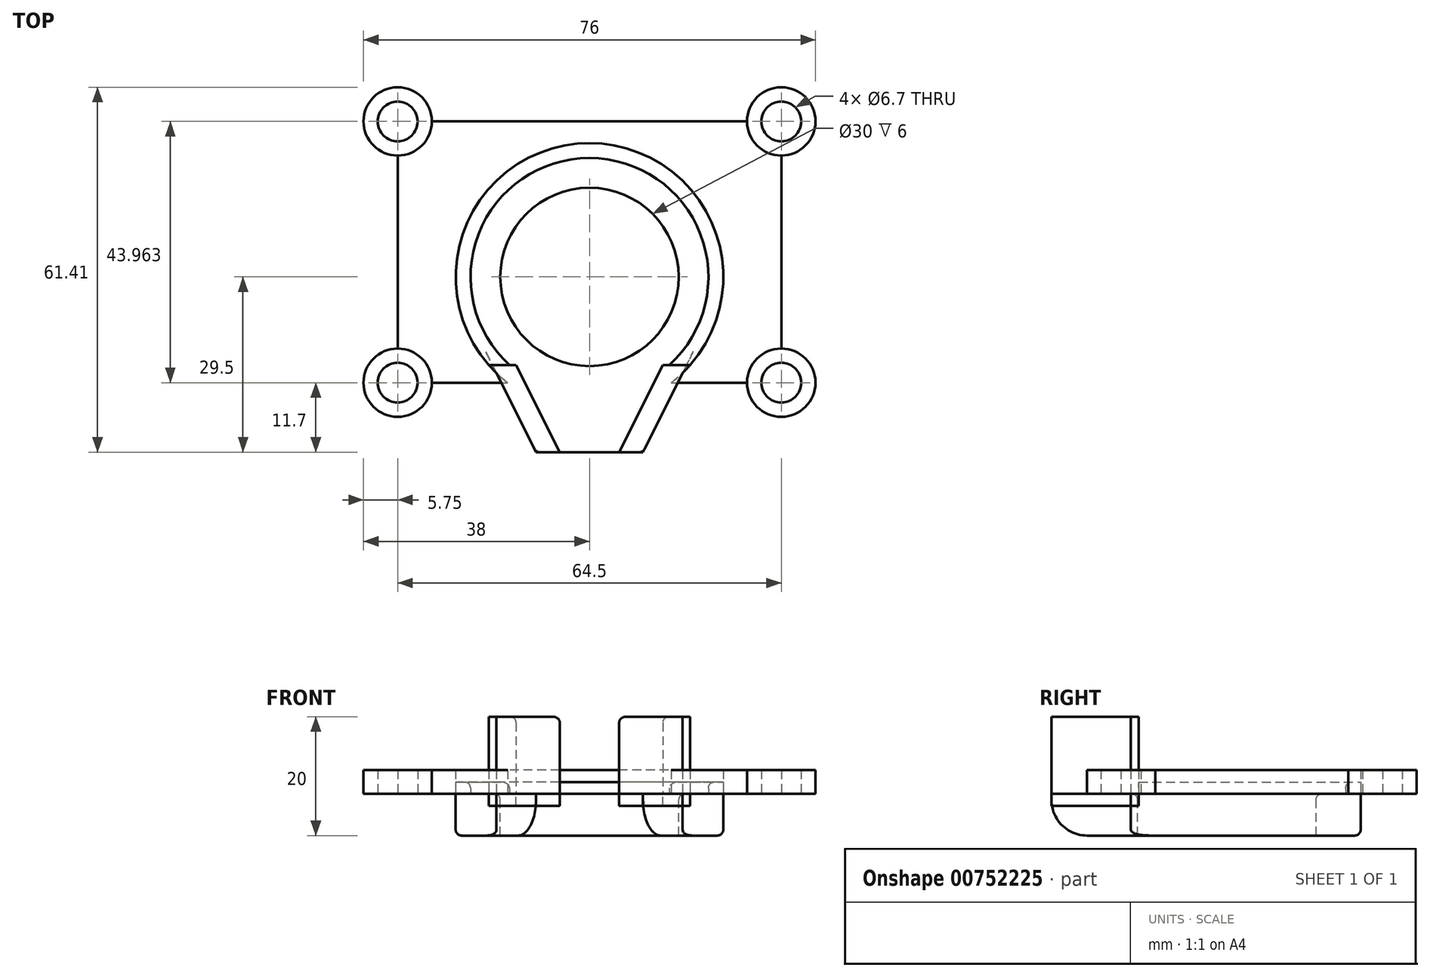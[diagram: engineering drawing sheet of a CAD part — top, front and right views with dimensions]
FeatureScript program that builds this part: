
annotation { "Feature Type Name" : "Feature", "Feature Type Description" : "" }
export const myFeature = defineFeature(function(context is Context, id is Id, definition is map)
    precondition{}
    {
        {
            var Q0;
            Q0=qCreatedBy(makeId("Top.planeOp"),FACE);
            var sketch = newSketch(context, id + "F0", { "sketchPlane" : qUnion([Q0])});
            skCircle(sketch, "E0", {"center": v(-32.25, 26.16) * mm, "radius": 5.75 * mm});
            skCircle(sketch, "E1", {"center": v(32.25, -17.8) * mm, "radius": 5.75 * mm});
            skCircle(sketch, "E2", {"center": v(32.25, -17.8) * mm, "radius": 3.35 * mm});
            skCircle(sketch, "E3", {"center": v(-32.25, 26.16) * mm, "radius": 3.35 * mm});
            skCircle(sketch, "E4", {"center": v(0, 0) * mm, "radius": 20 * mm});
            skCircle(sketch, "E5", {"center": v(0, 0) * mm, "radius": 15 * mm});
            skLineSegment(sketch, "E6", {"start": v(-32.25, -17.8) * mm, "end": v(32.25, -17.8) * mm});
            skCircle(sketch, "E7", {"center": v(-32.25, -17.8) * mm, "radius": 5.75 * mm});
            skCircle(sketch, "E8", {"center": v(-32.25, -17.8) * mm, "radius": 3.35 * mm});
            skLineSegment(sketch, "E9", {"start": v(-32.25, 26.16) * mm, "end": v(32.25, 26.16) * mm});
            skCircle(sketch, "E10", {"center": v(32.25, 26.16) * mm, "radius": 5.75 * mm});
            skCircle(sketch, "E11", {"center": v(32.25, 26.16) * mm, "radius": 3.35 * mm});
            skLineSegment(sketch, "E12", {"start": v(-5, -29.5) * mm, "end": v(5, -29.5) * mm});
            skLineSegment(sketch, "E13", {"start": v(-5, -29.5) * mm, "end": v(-9, -29.5) * mm});
            skLineSegment(sketch, "E14", {"start": v(5, -29.5) * mm, "end": v(9, -29.5) * mm});
            skLineSegment(sketch, "E15", {"start": v(-5, -29.5) * mm, "end": v(-12.33, -14.82) * mm});
            skLineSegment(sketch, "E16", {"start": v(-12.33, -14.82) * mm, "end": v(12.33, -14.82) * mm});
            skLineSegment(sketch, "E17", {"start": v(12.33, -14.82) * mm, "end": v(5, -29.5) * mm});
            skLineSegment(sketch, "E18", {"start": v(-12.33, -14.82) * mm, "end": v(-16.33, -14.82) * mm});
            skLineSegment(sketch, "E19", {"start": v(-16.33, -14.82) * mm, "end": v(-9, -29.5) * mm});
            skLineSegment(sketch, "E20", {"start": v(9, -29.5) * mm, "end": v(16.32, -14.82) * mm});
            skLineSegment(sketch, "E21", {"start": v(16.32, -14.82) * mm, "end": v(12.33, -14.82) * mm});
            skCircle(sketch, "E22", {"center": v(0, 0) * mm, "radius": 22.5 * mm});
            skLineSegment(sketch, "E23", {"start": v(-32.25, -17.8) * mm, "end": v(-32.25, 0) * mm});
            skLineSegment(sketch, "E24", {"start": v(-32.25, 0) * mm, "end": v(-32.25, 26.16) * mm});
            skLineSegment(sketch, "E25", {"start": v(-32.25, 26.16) * mm, "end": v(32.25, -17.8) * mm});
            skPoint(sketch, "E26.trimOffspring.end.orphan", {"position": v(0, -29.5) * mm});
            skLineSegment(sketch, "E27", {"start": v(0, -29.5) * mm, "end": v(0, 26.16) * mm});
            skLineSegment(sketch, "E28", {"start": v(32.25, 26.16) * mm, "end": v(32.25, 0) * mm});
            skLineSegment(sketch, "E29", {"start": v(32.25, 0) * mm, "end": v(32.25, -17.8) * mm});
            skLineSegment(sketch, "E30", {"start": v(-16.33, -14.82) * mm, "end": v(-16.93, -14.82) * mm});
            skLineSegment(sketch, "E31", {"start": v(16.32, -14.82) * mm, "end": v(16.93, -14.82) * mm});
            skSolve(sketch);
        }
        {
            var Q0;
            {var subQ0=sQuery(id+"F0.wireOp",EDGE,"E7");var subQ1=sQuery(id+"F0.wireOp",EDGE,"Wz8c8u1L-tIaJ-pxJv-zDBa-IqU4CHtZDm8W");var subQ2=makeQuery(id+"F0.imprint","INTERSECT",VERTEX,{"derivedFrom":[subQ1,subQ0]});Q0=makeQuery(id+"F0.imprint","IMPRINT",FACE,{"disambiguationData":[TD([[makeQuery(id+"F0.imprint","IMPRINT",EDGE,{"disambiguationData":[TD([[subQ2,-1.0]])],"derivedFrom":subQ1}),-1.0]])]});}
            var Q1;
            {var subQ0=sQuery(id+"F0.wireOp",EDGE,"E10");var subQ1=sQuery(id+"F0.wireOp",EDGE,"E9");var subQ2=makeQuery(id+"F0.imprint","INTERSECT",VERTEX,{"derivedFrom":[subQ1,subQ0]});Q1=makeQuery(id+"F0.imprint","IMPRINT",FACE,{"disambiguationData":[TD([[makeQuery(id+"F0.imprint","IMPRINT",EDGE,{"disambiguationData":[TD([[subQ2,-1.0]])],"derivedFrom":subQ1}),1.0]])]});}
            var Q2;
            {var subQ0=sQuery(id+"F0.wireOp",EDGE,"Wz8c8u1L-tIaJ-pxJv-zDBa-IqU4CHtZDm8W");var subQ1=sQuery(id+"F0.wireOp",EDGE,"E0");var subQ2=makeQuery(id+"F0.imprint","INTERSECT",VERTEX,{"derivedFrom":[subQ1,subQ0]});Q2=makeQuery(id+"F0.imprint","IMPRINT",FACE,{"disambiguationData":[TD([[makeQuery(id+"F0.imprint","IMPRINT",EDGE,{"disambiguationData":[TD([[subQ2,1.0]])],"derivedFrom":subQ1}),1.0]])]});}
            var Q3;
            {var subQ0=sQuery(id+"F0.wireOp",EDGE,"lU8kgJ5v-FxIN-fgI9-XZON-ElkpLmHzZSri");var subQ1=sQuery(id+"F0.wireOp",EDGE,"E1");var subQ2=makeQuery(id+"F0.imprint","INTERSECT",VERTEX,{"derivedFrom":[subQ1,subQ0]});Q3=makeQuery(id+"F0.imprint","IMPRINT",FACE,{"disambiguationData":[TD([[makeQuery(id+"F0.imprint","IMPRINT",EDGE,{"disambiguationData":[TD([[subQ2,1.0]])],"derivedFrom":subQ1}),1.0]])]});}
            var Q4;
            {var subQ0=sQuery(id+"F0.wireOp",EDGE,"E7");var subQ1=sQuery(id+"F0.wireOp",EDGE,"Wz8c8u1L-tIaJ-pxJv-zDBa-IqU4CHtZDm8W");var subQ2=makeQuery(id+"F0.imprint","INTERSECT",VERTEX,{"derivedFrom":[subQ1,subQ0]});Q4=makeQuery(id+"F0.imprint","IMPRINT",FACE,{"disambiguationData":[TD([[makeQuery(id+"F0.imprint","IMPRINT",EDGE,{"disambiguationData":[TD([[subQ2,-1.0]])],"derivedFrom":subQ1}),1.0]])]});}
            var Q5;
            {var subQ0=sQuery(id+"F0.wireOp",EDGE,"E10");var subQ1=sQuery(id+"F0.wireOp",EDGE,"E9");var subQ2=makeQuery(id+"F0.imprint","INTERSECT",VERTEX,{"derivedFrom":[subQ1,subQ0]});Q5=makeQuery(id+"F0.imprint","IMPRINT",FACE,{"disambiguationData":[TD([[makeQuery(id+"F0.imprint","IMPRINT",EDGE,{"disambiguationData":[TD([[subQ2,-1.0]])],"derivedFrom":subQ1}),-1.0]])]});}
            var Q6;
            {var subQ0=sQuery(id+"F0.wireOp",EDGE,"Wz8c8u1L-tIaJ-pxJv-zDBa-IqU4CHtZDm8W");var subQ1=sQuery(id+"F0.wireOp",EDGE,"E0");var subQ2=makeQuery(id+"F0.imprint","INTERSECT",VERTEX,{"derivedFrom":[subQ1,subQ0]});Q6=makeQuery(id+"F0.imprint","IMPRINT",FACE,{"disambiguationData":[TD([[makeQuery(id+"F0.imprint","IMPRINT",EDGE,{"disambiguationData":[TD([[subQ2,-1.0]])],"derivedFrom":subQ1}),1.0]])]});}
            var Q7;
            {var subQ0=sQuery(id+"F0.wireOp",EDGE,"E9");var subQ1=sQuery(id+"F0.wireOp",EDGE,"E0");var subQ2=makeQuery(id+"F0.imprint","INTERSECT",VERTEX,{"derivedFrom":[subQ1,subQ0]});Q7=makeQuery(id+"F0.imprint","IMPRINT",FACE,{"disambiguationData":[TD([[makeQuery(id+"F0.imprint","IMPRINT",EDGE,{"disambiguationData":[TD([[subQ2,1.0]])],"derivedFrom":subQ1}),1.0]])]});}
            var Q8;
            {var subQ0=sQuery(id+"F0.wireOp",EDGE,"lU8kgJ5v-FxIN-fgI9-XZON-ElkpLmHzZSri");var subQ1=sQuery(id+"F0.wireOp",EDGE,"E1");var subQ2=makeQuery(id+"F0.imprint","INTERSECT",VERTEX,{"derivedFrom":[subQ1,subQ0]});Q8=makeQuery(id+"F0.imprint","IMPRINT",FACE,{"disambiguationData":[TD([[makeQuery(id+"F0.imprint","IMPRINT",EDGE,{"disambiguationData":[TD([[subQ2,-1.0]])],"derivedFrom":subQ1}),1.0]])]});}
            var Q9;
            {var subQ0=sQuery(id+"F0.wireOp",EDGE,"E6");var subQ1=sQuery(id+"F0.wireOp",EDGE,"E1");var subQ2=makeQuery(id+"F0.imprint","INTERSECT",VERTEX,{"derivedFrom":[subQ1,subQ0]});Q9=makeQuery(id+"F0.imprint","IMPRINT",FACE,{"disambiguationData":[TD([[makeQuery(id+"F0.imprint","IMPRINT",EDGE,{"disambiguationData":[TD([[subQ2,1.0]])],"derivedFrom":subQ1}),1.0]])]});}
            var Q10;
            {var subQ0=sQuery(id+"F0.wireOp",EDGE,"E7");var subQ1=sQuery(id+"F0.wireOp",EDGE,"E6");var subQ2=makeQuery(id+"F0.imprint","INTERSECT",VERTEX,{"derivedFrom":[subQ1,subQ0]});Q10=makeQuery(id+"F0.imprint","IMPRINT",FACE,{"disambiguationData":[TD([[makeQuery(id+"F0.imprint","IMPRINT",EDGE,{"disambiguationData":[TD([[subQ2,1.0]])],"derivedFrom":subQ1}),-1.0]])]});}
            var Q11;
            {var subQ0=sQuery(id+"F0.wireOp",EDGE,"E7");var subQ1=sQuery(id+"F0.wireOp",EDGE,"E6");var subQ2=makeQuery(id+"F0.imprint","INTERSECT",VERTEX,{"derivedFrom":[subQ1,subQ0]});Q11=makeQuery(id+"F0.imprint","IMPRINT",FACE,{"disambiguationData":[TD([[makeQuery(id+"F0.imprint","IMPRINT",EDGE,{"disambiguationData":[TD([[subQ2,1.0]])],"derivedFrom":subQ1}),1.0]])]});}
            extrude(context, id + "F1", {"entities" : qUnion([Q0, Q1, Q2, Q3, Q4, Q5, Q6, Q7, Q8, Q9, Q10, Q11]), "depth" : 4 * mm, "offsetDistance" : 25 * mm});
        }
        {
            var Q0;
            {var subQ5=sQuery(id+"F0.wireOp",EDGE,"Wz8c8u1L-tIaJ-pxJv-zDBa-IqU4CHtZDm8W");var subQ6=sQuery(id+"F0.wireOp",EDGE,"E0");var subQ7=makeQuery(id+"F0.imprint","INTERSECT",VERTEX,{"derivedFrom":[subQ6,subQ5]});Q0=makeQuery(id+"F0.imprint","IMPRINT",FACE,{"disambiguationData":[TD([[makeQuery(id+"F0.imprint","IMPRINT",EDGE,{"disambiguationData":[TD([[subQ7,-1.0]])],"derivedFrom":subQ6}),-1.0]])]});}
            var Q1;
            {var subQ5=sQuery(id+"F0.wireOp",EDGE,"E0");var subQ10=sQuery(id+"F0.wireOp",EDGE,"E9");var subQ11=makeQuery(id+"F0.imprint","INTERSECT",VERTEX,{"derivedFrom":[subQ5,subQ10]});Q1=makeQuery(id+"F0.imprint","IMPRINT",FACE,{"disambiguationData":[TD([[makeQuery(id+"F0.imprint","IMPRINT",EDGE,{"disambiguationData":[TD([[subQ11,1.0]])],"derivedFrom":subQ5}),-1.0]])]});}
            var Q2;
            {var subQ1=sQuery(id+"F0.wireOp",EDGE,"E6");var subQ5=sQuery(id+"F0.wireOp",EDGE,"E1");var subQ6=makeQuery(id+"F0.imprint","INTERSECT",VERTEX,{"derivedFrom":[subQ5,subQ1]});Q2=makeQuery(id+"F0.imprint","IMPRINT",FACE,{"disambiguationData":[TD([[makeQuery(id+"F0.imprint","IMPRINT",EDGE,{"disambiguationData":[TD([[subQ6,1.0]])],"derivedFrom":subQ5}),-1.0]])]});}
            var Q3;
            {var subQ0=sQuery(id+"F0.wireOp",EDGE,"E19");var subQ1=sQuery(id+"F0.wireOp",EDGE,"E6");var subQ2=makeQuery(id+"F0.imprint","INTERSECT",VERTEX,{"derivedFrom":[subQ1,subQ0]});Q3=makeQuery(id+"F0.imprint","IMPRINT",FACE,{"disambiguationData":[TD([[makeQuery(id+"F0.imprint","IMPRINT",EDGE,{"disambiguationData":[TD([[subQ2,-1.0]])],"derivedFrom":subQ1}),1.0]])]});}
            var Q4;
            {var subQ9=sQuery(id+"F0.wireOp",EDGE,"E24");var subQ10=sQuery(id+"F0.wireOp",EDGE,"E0");var subQ11=makeQuery(id+"F0.imprint","INTERSECT",VERTEX,{"derivedFrom":[subQ10,subQ9]});Q4=makeQuery(id+"F0.imprint","IMPRINT",FACE,{"disambiguationData":[TD([[makeQuery(id+"F0.imprint","IMPRINT",EDGE,{"disambiguationData":[TD([[subQ11,-1.0]])],"derivedFrom":subQ10}),-1.0]])]});}
            var Q5;
            {var subQ5=sQuery(id+"F0.wireOp",EDGE,"E29");var subQ6=sQuery(id+"F0.wireOp",EDGE,"E1");var subQ7=makeQuery(id+"F0.imprint","INTERSECT",VERTEX,{"derivedFrom":[subQ6,subQ5]});Q5=makeQuery(id+"F0.imprint","IMPRINT",FACE,{"disambiguationData":[TD([[makeQuery(id+"F0.imprint","IMPRINT",EDGE,{"disambiguationData":[TD([[subQ7,-1.0]])],"derivedFrom":subQ6}),-1.0]])]});}
            var Q6;
            {var subQ0=sQuery(id+"F0.wireOp",EDGE,"E20");var subQ1=sQuery(id+"F0.wireOp",EDGE,"E6");var subQ2=makeQuery(id+"F0.imprint","INTERSECT",VERTEX,{"derivedFrom":[subQ1,subQ0]});Q6=makeQuery(id+"F0.imprint","IMPRINT",FACE,{"disambiguationData":[TD([[makeQuery(id+"F0.imprint","IMPRINT",EDGE,{"disambiguationData":[TD([[subQ2,1.0]])],"derivedFrom":subQ1}),1.0]])]});}
            extrude(context, id + "F2", {"entities" : qUnion([Q0, Q1, Q2, Q3, Q4, Q5, Q6]), "depth" : 4 * mm, "offsetDistance" : 25 * mm});
        }
        {
            var Q0;
            {var subQ5=sQuery(id+"F0.wireOp",EDGE,"E30");Q0=makeQuery(id+"F0.imprint","IMPRINT",FACE,{"disambiguationData":[TD([[makeQuery(id+"F0.imprint","IMPRINT",EDGE,{"derivedFrom":subQ5}),-1.0]])]});}
            var Q1;
            {var subQ3=sQuery(id+"F0.wireOp",EDGE,"E4");var subQ7=sQuery(id+"F0.wireOp",EDGE,"E25");var subQ9=makeQuery(id+"F0.imprint","INTERSECT",VERTEX,{"disambiguationData":[OD(0.0)],"derivedFrom":[subQ3,subQ7]});Q1=makeQuery(id+"F0.imprint","IMPRINT",FACE,{"disambiguationData":[TD([[makeQuery(id+"F0.imprint","IMPRINT",EDGE,{"disambiguationData":[TD([[subQ9,-1.0]])],"derivedFrom":subQ3}),1.0]])]});}
            var Q2;
            {var subQ0=sQuery(id+"F0.wireOp",EDGE,"E25");var subQ1=sQuery(id+"F0.wireOp",EDGE,"E4");var subQ2=makeQuery(id+"F0.imprint","INTERSECT",VERTEX,{"disambiguationData":[OD(0.0)],"derivedFrom":[subQ1,subQ0]});Q2=makeQuery(id+"F0.imprint","IMPRINT",FACE,{"disambiguationData":[TD([[makeQuery(id+"F0.imprint","IMPRINT",EDGE,{"disambiguationData":[TD([[subQ2,1.0]])],"derivedFrom":subQ1}),-1.0]])]});}
            var Q3;
            {var subQ0=sQuery(id+"F0.wireOp",EDGE,"E27");var subQ1=sQuery(id+"F0.wireOp",EDGE,"E4");var subQ2=makeQuery(id+"F0.imprint","INTERSECT",VERTEX,{"disambiguationData":[OD(0.0)],"derivedFrom":[subQ1,subQ0]});Q3=makeQuery(id+"F0.imprint","IMPRINT",FACE,{"disambiguationData":[TD([[makeQuery(id+"F0.imprint","IMPRINT",EDGE,{"disambiguationData":[TD([[subQ2,1.0]])],"derivedFrom":subQ1}),-1.0]])]});}
            var Q4;
            {var subQ0=sQuery(id+"F0.wireOp",EDGE,"E27");var subQ1=sQuery(id+"F0.wireOp",EDGE,"E4");var subQ2=makeQuery(id+"F0.imprint","INTERSECT",VERTEX,{"disambiguationData":[OD(0.0)],"derivedFrom":[subQ1,subQ0]});Q4=makeQuery(id+"F0.imprint","IMPRINT",FACE,{"disambiguationData":[TD([[makeQuery(id+"F0.imprint","IMPRINT",EDGE,{"disambiguationData":[TD([[subQ2,1.0]])],"derivedFrom":subQ1}),1.0]])]});}
            var Q5;
            {var subQ0=sQuery(id+"F0.wireOp",EDGE,"E25");var subQ1=sQuery(id+"F0.wireOp",EDGE,"E4");var subQ2=makeQuery(id+"F0.imprint","INTERSECT",VERTEX,{"disambiguationData":[OD(0.0)],"derivedFrom":[subQ1,subQ0]});Q5=makeQuery(id+"F0.imprint","IMPRINT",FACE,{"disambiguationData":[TD([[makeQuery(id+"F0.imprint","IMPRINT",EDGE,{"disambiguationData":[TD([[subQ2,1.0]])],"derivedFrom":subQ1}),1.0]])]});}
            var Q6;
            {var subQ0=sQuery(id+"F0.wireOp",EDGE,"E21");var subQ5=sQuery(id+"F0.wireOp",EDGE,"E4");var subQ6=makeQuery(id+"F0.imprint","INTERSECT",VERTEX,{"derivedFrom":[subQ5,subQ0]});Q6=makeQuery(id+"F0.imprint","IMPRINT",FACE,{"disambiguationData":[TD([[makeQuery(id+"F0.imprint","IMPRINT",EDGE,{"disambiguationData":[TD([[subQ6,-1.0]])],"derivedFrom":subQ5}),1.0]])]});}
            var Q7;
            {var subQ7=sQuery(id+"F0.wireOp",EDGE,"E31");Q7=makeQuery(id+"F0.imprint","IMPRINT",FACE,{"disambiguationData":[TD([[makeQuery(id+"F0.imprint","IMPRINT",EDGE,{"derivedFrom":subQ7}),1.0]])]});}
            var Q8;
            {var subQ1=sQuery(id+"F0.wireOp",EDGE,"E15");var subQ3=sQuery(id+"F0.wireOp",EDGE,"E4");var subQ4=makeQuery(id+"F0.imprint","INTERSECT",VERTEX,{"derivedFrom":[subQ3,subQ1]});Q8=makeQuery(id+"F0.imprint","IMPRINT",FACE,{"disambiguationData":[TD([[makeQuery(id+"F0.imprint","IMPRINT",EDGE,{"disambiguationData":[TD([[subQ4,-1.0]])],"derivedFrom":subQ3}),1.0]])]});}
            var Q9;
            {var subQ5=sQuery(id+"F0.wireOp",EDGE,"E6");var subQ6=sQuery(id+"F0.wireOp",EDGE,"E4");var subQ7=makeQuery(id+"F0.imprint","INTERSECT",VERTEX,{"disambiguationData":[OD(1.0)],"derivedFrom":[subQ6,subQ5]});Q9=makeQuery(id+"F0.imprint","IMPRINT",FACE,{"disambiguationData":[TD([[makeQuery(id+"F0.imprint","IMPRINT",EDGE,{"disambiguationData":[TD([[subQ7,-1.0]])],"derivedFrom":subQ6}),1.0]])]});}
            var Q10;
            {var subQ1=sQuery(id+"F0.wireOp",EDGE,"E18");var subQ3=sQuery(id+"F0.wireOp",EDGE,"E4");var subQ4=makeQuery(id+"F0.imprint","INTERSECT",VERTEX,{"derivedFrom":[subQ3,subQ1]});Q10=makeQuery(id+"F0.imprint","IMPRINT",FACE,{"disambiguationData":[TD([[makeQuery(id+"F0.imprint","IMPRINT",EDGE,{"disambiguationData":[TD([[subQ4,-1.0]])],"derivedFrom":subQ3}),-1.0]])]});}
            var Q11;
            {var subQ0=sQuery(id+"F0.wireOp",EDGE,"E18");var subQ1=sQuery(id+"F0.wireOp",EDGE,"E4");var subQ2=makeQuery(id+"F0.imprint","INTERSECT",VERTEX,{"derivedFrom":[subQ1,subQ0]});Q11=makeQuery(id+"F0.imprint","IMPRINT",FACE,{"disambiguationData":[TD([[makeQuery(id+"F0.imprint","IMPRINT",EDGE,{"disambiguationData":[TD([[subQ2,-1.0]])],"derivedFrom":subQ1}),1.0]])]});}
            var Q12;
            {var subQ0=sQuery(id+"F0.wireOp",EDGE,"E30");Q12=makeQuery(id+"F0.imprint","IMPRINT",FACE,{"disambiguationData":[TD([[makeQuery(id+"F0.imprint","IMPRINT",EDGE,{"derivedFrom":subQ0}),1.0]])]});}
            var Q13;
            {var subQ0=sQuery(id+"F0.wireOp",EDGE,"E15");var subQ1=sQuery(id+"F0.wireOp",EDGE,"E4");var subQ2=makeQuery(id+"F0.imprint","INTERSECT",VERTEX,{"derivedFrom":[subQ1,subQ0]});Q13=makeQuery(id+"F0.imprint","IMPRINT",FACE,{"disambiguationData":[TD([[makeQuery(id+"F0.imprint","IMPRINT",EDGE,{"disambiguationData":[TD([[subQ2,-1.0]])],"derivedFrom":subQ1}),-1.0]])]});}
            var Q14;
            {var subQ5=sQuery(id+"F0.wireOp",EDGE,"E6");var subQ6=sQuery(id+"F0.wireOp",EDGE,"E4");var subQ7=makeQuery(id+"F0.imprint","INTERSECT",VERTEX,{"disambiguationData":[OD(0.0)],"derivedFrom":[subQ6,subQ5]});Q14=makeQuery(id+"F0.imprint","IMPRINT",FACE,{"disambiguationData":[TD([[makeQuery(id+"F0.imprint","IMPRINT",EDGE,{"disambiguationData":[TD([[subQ7,-1.0]])],"derivedFrom":subQ6}),-1.0]])]});}
            var Q15;
            {var subQ0=sQuery(id+"F0.wireOp",EDGE,"E6");var subQ1=sQuery(id+"F0.wireOp",EDGE,"E4");var subQ2=makeQuery(id+"F0.imprint","INTERSECT",VERTEX,{"disambiguationData":[OD(0.0)],"derivedFrom":[subQ1,subQ0]});Q15=makeQuery(id+"F0.imprint","IMPRINT",FACE,{"disambiguationData":[TD([[makeQuery(id+"F0.imprint","IMPRINT",EDGE,{"disambiguationData":[TD([[subQ2,-1.0]])],"derivedFrom":subQ1}),1.0]])]});}
            var Q16;
            {var subQ0=sQuery(id+"F0.wireOp",EDGE,"E22");var subQ1=sQuery(id+"F0.wireOp",EDGE,"E6");var subQ2=makeQuery(id+"F0.imprint","INTERSECT",VERTEX,{"disambiguationData":[OD(0.0)],"derivedFrom":[subQ1,subQ0]});Q16=makeQuery(id+"F0.imprint","IMPRINT",FACE,{"disambiguationData":[TD([[makeQuery(id+"F0.imprint","IMPRINT",EDGE,{"disambiguationData":[TD([[subQ2,-1.0]])],"derivedFrom":subQ1}),-1.0]])]});}
            var Q17;
            {var subQ1=sQuery(id+"F0.wireOp",EDGE,"E13");Q17=makeQuery(id+"F0.imprint","IMPRINT",FACE,{"disambiguationData":[TD([[makeQuery(id+"F0.imprint","IMPRINT",EDGE,{"derivedFrom":subQ1}),-1.0]])]});}
            var Q18;
            {var subQ0=sQuery(id+"F0.wireOp",EDGE,"E15");var subQ5=sQuery(id+"F0.wireOp",EDGE,"E22");var subQ6=makeQuery(id+"F0.imprint","INTERSECT",VERTEX,{"derivedFrom":[subQ0,subQ5]});Q18=makeQuery(id+"F0.imprint","IMPRINT",FACE,{"disambiguationData":[TD([[makeQuery(id+"F0.imprint","IMPRINT",EDGE,{"disambiguationData":[TD([[subQ6,-1.0]])],"derivedFrom":subQ5}),-1.0]])]});}
            var Q19;
            {var subQ3=sQuery(id+"F0.wireOp",EDGE,"E27");var subQ7=sQuery(id+"F0.wireOp",EDGE,"E4");var subQ9=makeQuery(id+"F0.imprint","INTERSECT",VERTEX,{"disambiguationData":[OD(1.0)],"derivedFrom":[subQ7,subQ3]});Q19=makeQuery(id+"F0.imprint","IMPRINT",FACE,{"disambiguationData":[TD([[makeQuery(id+"F0.imprint","IMPRINT",EDGE,{"disambiguationData":[TD([[subQ9,-1.0]])],"derivedFrom":subQ7}),-1.0]])]});}
            var Q20;
            {var subQ0=sQuery(id+"F0.wireOp",EDGE,"E27");var subQ1=sQuery(id+"F0.wireOp",EDGE,"E4");var subQ2=makeQuery(id+"F0.imprint","INTERSECT",VERTEX,{"disambiguationData":[OD(1.0)],"derivedFrom":[subQ1,subQ0]});Q20=makeQuery(id+"F0.imprint","IMPRINT",FACE,{"disambiguationData":[TD([[makeQuery(id+"F0.imprint","IMPRINT",EDGE,{"disambiguationData":[TD([[subQ2,-1.0]])],"derivedFrom":subQ1}),1.0]])]});}
            var Q21;
            {var subQ0=sQuery(id+"F0.wireOp",EDGE,"E17");var subQ5=sQuery(id+"F0.wireOp",EDGE,"E22");var subQ7=makeQuery(id+"F0.imprint","INTERSECT",VERTEX,{"derivedFrom":[subQ0,subQ5]});Q21=makeQuery(id+"F0.imprint","IMPRINT",FACE,{"disambiguationData":[TD([[makeQuery(id+"F0.imprint","IMPRINT",EDGE,{"disambiguationData":[TD([[subQ7,1.0]])],"derivedFrom":subQ5}),-1.0]])]});}
            var Q22;
            {var subQ1=sQuery(id+"F0.wireOp",EDGE,"E14");Q22=makeQuery(id+"F0.imprint","IMPRINT",FACE,{"disambiguationData":[TD([[makeQuery(id+"F0.imprint","IMPRINT",EDGE,{"derivedFrom":subQ1}),1.0]])]});}
            var Q23;
            {var subQ0=sQuery(id+"F0.wireOp",EDGE,"E17");var subQ1=sQuery(id+"F0.wireOp",EDGE,"E6");var subQ2=makeQuery(id+"F0.imprint","INTERSECT",VERTEX,{"derivedFrom":[subQ1,subQ0]});Q23=makeQuery(id+"F0.imprint","IMPRINT",FACE,{"disambiguationData":[TD([[makeQuery(id+"F0.imprint","IMPRINT",EDGE,{"disambiguationData":[TD([[subQ2,-1.0]])],"derivedFrom":subQ1}),-1.0]])]});}
            var Q24;
            {var subQ0=sQuery(id+"F0.wireOp",EDGE,"E6");var subQ1=sQuery(id+"F0.wireOp",EDGE,"E4");var subQ2=makeQuery(id+"F0.imprint","INTERSECT",VERTEX,{"disambiguationData":[OD(1.0)],"derivedFrom":[subQ1,subQ0]});Q24=makeQuery(id+"F0.imprint","IMPRINT",FACE,{"disambiguationData":[TD([[makeQuery(id+"F0.imprint","IMPRINT",EDGE,{"disambiguationData":[TD([[subQ2,-1.0]])],"derivedFrom":subQ1}),-1.0]])]});}
            var Q25;
            {var subQ0=sQuery(id+"F0.wireOp",EDGE,"E17");var subQ9=sQuery(id+"F0.wireOp",EDGE,"E4");var subQ10=makeQuery(id+"F0.imprint","INTERSECT",VERTEX,{"derivedFrom":[subQ9,subQ0]});Q25=makeQuery(id+"F0.imprint","IMPRINT",FACE,{"disambiguationData":[TD([[makeQuery(id+"F0.imprint","IMPRINT",EDGE,{"disambiguationData":[TD([[subQ10,-1.0]])],"derivedFrom":subQ9}),-1.0]])]});}
            var Q26;
            {var subQ0=sQuery(id+"F0.wireOp",EDGE,"E17");var subQ1=sQuery(id+"F0.wireOp",EDGE,"E4");var subQ2=makeQuery(id+"F0.imprint","INTERSECT",VERTEX,{"derivedFrom":[subQ1,subQ0]});Q26=makeQuery(id+"F0.imprint","IMPRINT",FACE,{"disambiguationData":[TD([[makeQuery(id+"F0.imprint","IMPRINT",EDGE,{"disambiguationData":[TD([[subQ2,-1.0]])],"derivedFrom":subQ1}),1.0]])]});}
            var Q27;
            {var subQ0=sQuery(id+"F0.wireOp",EDGE,"E20");var subQ1=sQuery(id+"F0.wireOp",EDGE,"E6");var subQ2=makeQuery(id+"F0.imprint","INTERSECT",VERTEX,{"derivedFrom":[subQ1,subQ0]});Q27=makeQuery(id+"F0.imprint","IMPRINT",FACE,{"disambiguationData":[TD([[makeQuery(id+"F0.imprint","IMPRINT",EDGE,{"disambiguationData":[TD([[subQ2,1.0]])],"derivedFrom":subQ1}),1.0]])]});}
            var Q28;
            {var subQ0=sQuery(id+"F0.wireOp",EDGE,"E31");Q28=makeQuery(id+"F0.imprint","IMPRINT",FACE,{"disambiguationData":[TD([[makeQuery(id+"F0.imprint","IMPRINT",EDGE,{"derivedFrom":subQ0}),-1.0]])]});}
            var Q29;
            {var subQ0=sQuery(id+"F0.wireOp",EDGE,"E19");var subQ1=sQuery(id+"F0.wireOp",EDGE,"E6");var subQ2=makeQuery(id+"F0.imprint","INTERSECT",VERTEX,{"derivedFrom":[subQ1,subQ0]});Q29=makeQuery(id+"F0.imprint","IMPRINT",FACE,{"disambiguationData":[TD([[makeQuery(id+"F0.imprint","IMPRINT",EDGE,{"disambiguationData":[TD([[subQ2,-1.0]])],"derivedFrom":subQ1}),1.0]])]});}
            var Q30;
            {var subQ0=sQuery(id+"F0.wireOp",EDGE,"E16");var subQ5=sQuery(id+"F0.wireOp",EDGE,"E5");var subQ6=makeQuery(id+"F0.imprint","INTERSECT",VERTEX,{"disambiguationData":[OD(0.0)],"derivedFrom":[subQ5,subQ0]});Q30=makeQuery(id+"F0.imprint","IMPRINT",FACE,{"disambiguationData":[TD([[makeQuery(id+"F0.imprint","IMPRINT",EDGE,{"disambiguationData":[TD([[subQ6,-1.0]])],"derivedFrom":subQ5}),-1.0]])]});}
            var Q31;
            {var subQ5=sQuery(id+"F0.wireOp",EDGE,"E27");var subQ7=sQuery(id+"F0.wireOp",EDGE,"E5");var subQ9=makeQuery(id+"F0.imprint","INTERSECT",VERTEX,{"disambiguationData":[OD(1.0)],"derivedFrom":[subQ7,subQ5]});Q31=makeQuery(id+"F0.imprint","IMPRINT",FACE,{"disambiguationData":[TD([[makeQuery(id+"F0.imprint","IMPRINT",EDGE,{"disambiguationData":[TD([[subQ9,-1.0]])],"derivedFrom":subQ7}),-1.0]])]});}
            var Q32;
            {var subQ0=sQuery(id+"F0.wireOp",EDGE,"E22");var subQ1=sQuery(id+"F0.wireOp",EDGE,"E6");var subQ2=makeQuery(id+"F0.imprint","INTERSECT",VERTEX,{"disambiguationData":[OD(1.0)],"derivedFrom":[subQ1,subQ0]});Q32=makeQuery(id+"F0.imprint","IMPRINT",FACE,{"disambiguationData":[TD([[makeQuery(id+"F0.imprint","IMPRINT",EDGE,{"disambiguationData":[TD([[subQ2,1.0]])],"derivedFrom":subQ1}),-1.0]])]});}
            extrude(context, id + "F3", {"entities" : qUnion([Q0, Q1, Q2, Q3, Q4, Q5, Q6, Q7, Q8, Q9, Q10, Q11, Q12, Q13, Q14, Q15, Q16, Q17, Q18, Q19, Q20, Q21, Q22, Q23, Q24, Q25, Q26, Q27, Q28, Q29, Q30, Q31, Q32]), "depth" : -7 * mm, "offsetDistance" : 25 * mm});
        }
        {
            var Q0;
            {var subQ5=sQuery(id+"F0.wireOp",EDGE,"E30");Q0=makeQuery(id+"F0.imprint","IMPRINT",FACE,{"disambiguationData":[TD([[makeQuery(id+"F0.imprint","IMPRINT",EDGE,{"derivedFrom":subQ5}),-1.0]])]});}
            var Q1;
            {var subQ0=sQuery(id+"F0.wireOp",EDGE,"E25");var subQ1=sQuery(id+"F0.wireOp",EDGE,"E4");var subQ2=makeQuery(id+"F0.imprint","INTERSECT",VERTEX,{"disambiguationData":[OD(0.0)],"derivedFrom":[subQ1,subQ0]});Q1=makeQuery(id+"F0.imprint","IMPRINT",FACE,{"disambiguationData":[TD([[makeQuery(id+"F0.imprint","IMPRINT",EDGE,{"disambiguationData":[TD([[subQ2,1.0]])],"derivedFrom":subQ1}),-1.0]])]});}
            var Q2;
            {var subQ0=sQuery(id+"F0.wireOp",EDGE,"E27");var subQ1=sQuery(id+"F0.wireOp",EDGE,"E4");var subQ2=makeQuery(id+"F0.imprint","INTERSECT",VERTEX,{"disambiguationData":[OD(0.0)],"derivedFrom":[subQ1,subQ0]});Q2=makeQuery(id+"F0.imprint","IMPRINT",FACE,{"disambiguationData":[TD([[makeQuery(id+"F0.imprint","IMPRINT",EDGE,{"disambiguationData":[TD([[subQ2,1.0]])],"derivedFrom":subQ1}),-1.0]])]});}
            var Q3;
            {var subQ7=sQuery(id+"F0.wireOp",EDGE,"E31");Q3=makeQuery(id+"F0.imprint","IMPRINT",FACE,{"disambiguationData":[TD([[makeQuery(id+"F0.imprint","IMPRINT",EDGE,{"derivedFrom":subQ7}),1.0]])]});}
            extrude(context, id + "F4", {"entities" : qUnion([Q0, Q1, Q2, Q3]), "depth" : 2 * mm, "offsetDistance" : 25 * mm});
        }
        {
            var Q0;
            {var subQ0=sQuery(id+"F0.wireOp",EDGE,"E18");var subQ1=sQuery(id+"F0.wireOp",EDGE,"E4");var subQ2=makeQuery(id+"F0.imprint","INTERSECT",VERTEX,{"derivedFrom":[subQ1,subQ0]});Q0=makeQuery(id+"F0.imprint","IMPRINT",FACE,{"disambiguationData":[TD([[makeQuery(id+"F0.imprint","IMPRINT",EDGE,{"disambiguationData":[TD([[subQ2,-1.0]])],"derivedFrom":subQ1}),1.0]])]});}
            var Q1;
            {var subQ1=sQuery(id+"F0.wireOp",EDGE,"E18");var subQ3=sQuery(id+"F0.wireOp",EDGE,"E4");var subQ4=makeQuery(id+"F0.imprint","INTERSECT",VERTEX,{"derivedFrom":[subQ3,subQ1]});Q1=makeQuery(id+"F0.imprint","IMPRINT",FACE,{"disambiguationData":[TD([[makeQuery(id+"F0.imprint","IMPRINT",EDGE,{"disambiguationData":[TD([[subQ4,-1.0]])],"derivedFrom":subQ3}),-1.0]])]});}
            var Q2;
            {var subQ0=sQuery(id+"F0.wireOp",EDGE,"E30");Q2=makeQuery(id+"F0.imprint","IMPRINT",FACE,{"disambiguationData":[TD([[makeQuery(id+"F0.imprint","IMPRINT",EDGE,{"derivedFrom":subQ0}),1.0]])]});}
            var Q3;
            {var subQ0=sQuery(id+"F0.wireOp",EDGE,"E19");var subQ1=sQuery(id+"F0.wireOp",EDGE,"E6");var subQ2=makeQuery(id+"F0.imprint","INTERSECT",VERTEX,{"derivedFrom":[subQ1,subQ0]});Q3=makeQuery(id+"F0.imprint","IMPRINT",FACE,{"disambiguationData":[TD([[makeQuery(id+"F0.imprint","IMPRINT",EDGE,{"disambiguationData":[TD([[subQ2,-1.0]])],"derivedFrom":subQ1}),1.0]])]});}
            var Q4;
            {var subQ1=sQuery(id+"F0.wireOp",EDGE,"E13");Q4=makeQuery(id+"F0.imprint","IMPRINT",FACE,{"disambiguationData":[TD([[makeQuery(id+"F0.imprint","IMPRINT",EDGE,{"derivedFrom":subQ1}),-1.0]])]});}
            var Q5;
            {var subQ0=sQuery(id+"F0.wireOp",EDGE,"E22");var subQ1=sQuery(id+"F0.wireOp",EDGE,"E6");var subQ2=makeQuery(id+"F0.imprint","INTERSECT",VERTEX,{"disambiguationData":[OD(0.0)],"derivedFrom":[subQ1,subQ0]});Q5=makeQuery(id+"F0.imprint","IMPRINT",FACE,{"disambiguationData":[TD([[makeQuery(id+"F0.imprint","IMPRINT",EDGE,{"disambiguationData":[TD([[subQ2,-1.0]])],"derivedFrom":subQ1}),-1.0]])]});}
            var Q6;
            {var subQ1=sQuery(id+"F0.wireOp",EDGE,"E14");Q6=makeQuery(id+"F0.imprint","IMPRINT",FACE,{"disambiguationData":[TD([[makeQuery(id+"F0.imprint","IMPRINT",EDGE,{"derivedFrom":subQ1}),1.0]])]});}
            var Q7;
            {var subQ0=sQuery(id+"F0.wireOp",EDGE,"E17");var subQ1=sQuery(id+"F0.wireOp",EDGE,"E6");var subQ2=makeQuery(id+"F0.imprint","INTERSECT",VERTEX,{"derivedFrom":[subQ1,subQ0]});Q7=makeQuery(id+"F0.imprint","IMPRINT",FACE,{"disambiguationData":[TD([[makeQuery(id+"F0.imprint","IMPRINT",EDGE,{"disambiguationData":[TD([[subQ2,-1.0]])],"derivedFrom":subQ1}),-1.0]])]});}
            var Q8;
            {var subQ0=sQuery(id+"F0.wireOp",EDGE,"E17");var subQ9=sQuery(id+"F0.wireOp",EDGE,"E4");var subQ10=makeQuery(id+"F0.imprint","INTERSECT",VERTEX,{"derivedFrom":[subQ9,subQ0]});Q8=makeQuery(id+"F0.imprint","IMPRINT",FACE,{"disambiguationData":[TD([[makeQuery(id+"F0.imprint","IMPRINT",EDGE,{"disambiguationData":[TD([[subQ10,-1.0]])],"derivedFrom":subQ9}),-1.0]])]});}
            var Q9;
            {var subQ0=sQuery(id+"F0.wireOp",EDGE,"E31");Q9=makeQuery(id+"F0.imprint","IMPRINT",FACE,{"disambiguationData":[TD([[makeQuery(id+"F0.imprint","IMPRINT",EDGE,{"derivedFrom":subQ0}),-1.0]])]});}
            var Q10;
            {var subQ0=sQuery(id+"F0.wireOp",EDGE,"E17");var subQ1=sQuery(id+"F0.wireOp",EDGE,"E4");var subQ2=makeQuery(id+"F0.imprint","INTERSECT",VERTEX,{"derivedFrom":[subQ1,subQ0]});Q10=makeQuery(id+"F0.imprint","IMPRINT",FACE,{"disambiguationData":[TD([[makeQuery(id+"F0.imprint","IMPRINT",EDGE,{"disambiguationData":[TD([[subQ2,-1.0]])],"derivedFrom":subQ1}),1.0]])]});}
            var Q11;
            {var subQ0=sQuery(id+"F0.wireOp",EDGE,"E20");var subQ1=sQuery(id+"F0.wireOp",EDGE,"E6");var subQ2=makeQuery(id+"F0.imprint","INTERSECT",VERTEX,{"derivedFrom":[subQ1,subQ0]});Q11=makeQuery(id+"F0.imprint","IMPRINT",FACE,{"disambiguationData":[TD([[makeQuery(id+"F0.imprint","IMPRINT",EDGE,{"disambiguationData":[TD([[subQ2,1.0]])],"derivedFrom":subQ1}),1.0]])]});}
            var Q12;
            {var subQ0=sQuery(id+"F0.wireOp",EDGE,"E22");var subQ1=sQuery(id+"F0.wireOp",EDGE,"E6");var subQ2=makeQuery(id+"F0.imprint","INTERSECT",VERTEX,{"disambiguationData":[OD(1.0)],"derivedFrom":[subQ1,subQ0]});Q12=makeQuery(id+"F0.imprint","IMPRINT",FACE,{"disambiguationData":[TD([[makeQuery(id+"F0.imprint","IMPRINT",EDGE,{"disambiguationData":[TD([[subQ2,1.0]])],"derivedFrom":subQ1}),-1.0]])]});}
            extrude(context, id + "F5", {"entities" : qUnion([Q0, Q1, Q2, Q3, Q4, Q5, Q6, Q7, Q8, Q9, Q10, Q11, Q12]), "depth" : 13 * mm, "offsetDistance" : 25 * mm});
        }
        {
            var Q0;
            Q0=makeQuery(id+"F5.opExtrude","CAP_EDGE",EDGE,{"disambiguationData":[OSD([sQuery(id+"F0.wireOp",EDGE,"E15")])],"isStart":false});
            fillet(context, id + "F6", {"entities" : qUnion([Q0]), "radius" : 1 * mm, "tangentPropagation" : true, "allowEdgeOverflow" : false});
        }
        {
            var Q0;
            Q0=makeQuery(id+"F5.opExtrude","CAP_EDGE",EDGE,{"disambiguationData":[OSD([sQuery(id+"F0.wireOp",EDGE,"E17")])],"isStart":false});
            fillet(context, id + "F7", {"entities" : qUnion([Q0]), "radius" : 1 * mm, "tangentPropagation" : true, "allowEdgeOverflow" : false});
        }
        {
            var Q0;
            Q0=makeQuery(id+"F4.opExtrude","CAP_EDGE",EDGE,{"disambiguationData":[OSD([sQuery(id+"F0.wireOp",EDGE,"E4")])],"isStart":false});
            fillet(context, id + "F8", {"entities" : qUnion([Q0]), "radius" : 1 * mm, "tangentPropagation" : true, "allowEdgeOverflow" : false});
        }
        {
            var Q0;
            Q0=makeQuery(id+"F3.opExtrude","CAP_EDGE",EDGE,{"disambiguationData":[OSD([sQuery(id+"F0.wireOp",EDGE,"E5")])],"isStart":true});
            fillet(context, id + "F9", {"entities" : qUnion([Q0]), "radius" : 1 * mm, "tangentPropagation" : true, "allowEdgeOverflow" : false});
        }
        {
            var Q0;
            Q0=makeQuery(id+"F3.opExtrude","CAP_EDGE",EDGE,{"disambiguationData":[OSD([sQuery(id+"F0.wireOp",EDGE,"E12"),sQuery(id+"F0.wireOp",EDGE,"E13"),sQuery(id+"F0.wireOp",EDGE,"E14")])],"isStart":false});
            fillet(context, id + "F10", {"entities" : qUnion([Q0]), "radius" : 6 * mm, "tangentPropagation" : true, "allowEdgeOverflow" : false});
        }
        {
            var Q0;
            Q0=makeQuery(id+"F3.opExtrude","CAP_EDGE",EDGE,{"disambiguationData":[OSD([sQuery(id+"F0.wireOp",EDGE,"E22")])],"isStart":false});
            fillet(context, id + "F11", {"entities" : qUnion([Q0]), "radius" : 1 * mm, "tangentPropagation" : true, "allowEdgeOverflow" : false});
        }
        {
            var Q0;
            Q0=makeQuery(id+"F5.opExtrude","SWEPT_EDGE",EDGE,{"disambiguationData":[OSD([sQuery(id+"F0.wireOp",EDGE,"E14"),sQuery(id+"F0.wireOp",EDGE,"E20")])]});
            fillet(context, id + "F12", {"entities" : qUnion([Q0]), "radius" : 1 * mm, "tangentPropagation" : true, "allowEdgeOverflow" : false});
        }
        {
            var Q0;
            Q0=makeQuery(id+"F5.opExtrude","SWEPT_EDGE",EDGE,{"disambiguationData":[OSD([sQuery(id+"F0.wireOp",EDGE,"E13"),sQuery(id+"F0.wireOp",EDGE,"E19")])]});
            fillet(context, id + "F13", {"entities" : qUnion([Q0]), "radius" : 1 * mm, "tangentPropagation" : true, "allowEdgeOverflow" : false});
        }
        {
            var Q0;
            {var subQ1=sQuery(id+"F0.wireOp",EDGE,"E13");Q0=makeQuery(id+"F0.imprint","IMPRINT",FACE,{"disambiguationData":[TD([[makeQuery(id+"F0.imprint","IMPRINT",EDGE,{"derivedFrom":subQ1}),-1.0]])]});}
            var Q1;
            {var subQ1=sQuery(id+"F0.wireOp",EDGE,"E14");Q1=makeQuery(id+"F0.imprint","IMPRINT",FACE,{"disambiguationData":[TD([[makeQuery(id+"F0.imprint","IMPRINT",EDGE,{"derivedFrom":subQ1}),1.0]])]});}
            var Q2;
            {var subQ0=sQuery(id+"F0.wireOp",EDGE,"E17");var subQ1=sQuery(id+"F0.wireOp",EDGE,"E6");var subQ2=makeQuery(id+"F0.imprint","INTERSECT",VERTEX,{"derivedFrom":[subQ1,subQ0]});Q2=makeQuery(id+"F0.imprint","IMPRINT",FACE,{"disambiguationData":[TD([[makeQuery(id+"F0.imprint","IMPRINT",EDGE,{"disambiguationData":[TD([[subQ2,-1.0]])],"derivedFrom":subQ1}),-1.0]])]});}
            var Q3;
            {var subQ0=sQuery(id+"F0.wireOp",EDGE,"E17");var subQ9=sQuery(id+"F0.wireOp",EDGE,"E4");var subQ10=makeQuery(id+"F0.imprint","INTERSECT",VERTEX,{"derivedFrom":[subQ9,subQ0]});Q3=makeQuery(id+"F0.imprint","IMPRINT",FACE,{"disambiguationData":[TD([[makeQuery(id+"F0.imprint","IMPRINT",EDGE,{"disambiguationData":[TD([[subQ10,-1.0]])],"derivedFrom":subQ9}),-1.0]])]});}
            var Q4;
            {var subQ0=sQuery(id+"F0.wireOp",EDGE,"E31");Q4=makeQuery(id+"F0.imprint","IMPRINT",FACE,{"disambiguationData":[TD([[makeQuery(id+"F0.imprint","IMPRINT",EDGE,{"derivedFrom":subQ0}),-1.0]])]});}
            var Q5;
            {var subQ0=sQuery(id+"F0.wireOp",EDGE,"E20");var subQ1=sQuery(id+"F0.wireOp",EDGE,"E6");var subQ2=makeQuery(id+"F0.imprint","INTERSECT",VERTEX,{"derivedFrom":[subQ1,subQ0]});Q5=makeQuery(id+"F0.imprint","IMPRINT",FACE,{"disambiguationData":[TD([[makeQuery(id+"F0.imprint","IMPRINT",EDGE,{"disambiguationData":[TD([[subQ2,1.0]])],"derivedFrom":subQ1}),1.0]])]});}
            var Q6;
            {var subQ0=sQuery(id+"F0.wireOp",EDGE,"E17");var subQ1=sQuery(id+"F0.wireOp",EDGE,"E4");var subQ2=makeQuery(id+"F0.imprint","INTERSECT",VERTEX,{"derivedFrom":[subQ1,subQ0]});Q6=makeQuery(id+"F0.imprint","IMPRINT",FACE,{"disambiguationData":[TD([[makeQuery(id+"F0.imprint","IMPRINT",EDGE,{"disambiguationData":[TD([[subQ2,-1.0]])],"derivedFrom":subQ1}),1.0]])]});}
            var Q7;
            {var subQ0=sQuery(id+"F0.wireOp",EDGE,"E22");var subQ1=sQuery(id+"F0.wireOp",EDGE,"E6");var subQ2=makeQuery(id+"F0.imprint","INTERSECT",VERTEX,{"disambiguationData":[OD(0.0)],"derivedFrom":[subQ1,subQ0]});Q7=makeQuery(id+"F0.imprint","IMPRINT",FACE,{"disambiguationData":[TD([[makeQuery(id+"F0.imprint","IMPRINT",EDGE,{"disambiguationData":[TD([[subQ2,-1.0]])],"derivedFrom":subQ1}),-1.0]])]});}
            var Q8;
            {var subQ1=sQuery(id+"F0.wireOp",EDGE,"E18");var subQ3=sQuery(id+"F0.wireOp",EDGE,"E4");var subQ4=makeQuery(id+"F0.imprint","INTERSECT",VERTEX,{"derivedFrom":[subQ3,subQ1]});Q8=makeQuery(id+"F0.imprint","IMPRINT",FACE,{"disambiguationData":[TD([[makeQuery(id+"F0.imprint","IMPRINT",EDGE,{"disambiguationData":[TD([[subQ4,-1.0]])],"derivedFrom":subQ3}),-1.0]])]});}
            var Q9;
            {var subQ0=sQuery(id+"F0.wireOp",EDGE,"E18");var subQ1=sQuery(id+"F0.wireOp",EDGE,"E4");var subQ2=makeQuery(id+"F0.imprint","INTERSECT",VERTEX,{"derivedFrom":[subQ1,subQ0]});Q9=makeQuery(id+"F0.imprint","IMPRINT",FACE,{"disambiguationData":[TD([[makeQuery(id+"F0.imprint","IMPRINT",EDGE,{"disambiguationData":[TD([[subQ2,-1.0]])],"derivedFrom":subQ1}),1.0]])]});}
            var Q10;
            {var subQ0=sQuery(id+"F0.wireOp",EDGE,"E19");var subQ1=sQuery(id+"F0.wireOp",EDGE,"E6");var subQ2=makeQuery(id+"F0.imprint","INTERSECT",VERTEX,{"derivedFrom":[subQ1,subQ0]});Q10=makeQuery(id+"F0.imprint","IMPRINT",FACE,{"disambiguationData":[TD([[makeQuery(id+"F0.imprint","IMPRINT",EDGE,{"disambiguationData":[TD([[subQ2,-1.0]])],"derivedFrom":subQ1}),1.0]])]});}
            var Q11;
            {var subQ0=sQuery(id+"F0.wireOp",EDGE,"E30");Q11=makeQuery(id+"F0.imprint","IMPRINT",FACE,{"disambiguationData":[TD([[makeQuery(id+"F0.imprint","IMPRINT",EDGE,{"derivedFrom":subQ0}),1.0]])]});}
            extrude(context, id + "F14", {"entities" : qUnion([Q0, Q1, Q2, Q3, Q4, Q5, Q6, Q7, Q8, Q9, Q10, Q11]), "depth" : -2 * mm, "offsetDistance" : 25 * mm});
        }
    });
